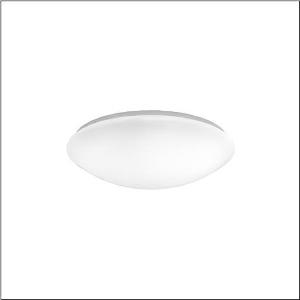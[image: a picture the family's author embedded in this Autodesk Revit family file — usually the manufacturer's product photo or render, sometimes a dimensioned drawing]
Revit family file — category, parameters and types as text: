
# Revit family: round_31_b_5pja130001a
name_source: partatom
category: Lighting Fixtures
units: mm (PartAtom-declared; Revit-internal decimal feet)

## family parameters
Cut with Voids When Loaded = No
Host = Face
Light Source = No
Part Type = Normal
Room Calculation Point = No
Round Connector Dimension = Use Diameter
Shared = No

## types (1)
- Round 31 B (1 x LED, 2700 lm, 21 W, 4000K)
    Apparent Load = 21 VA
    CIE Flux Codes = 42 71 89 88 100
    Color Rendering = 80
    Color Temperature = 4000K
    Default Elevation = 1800 mm
    Description = Round 31 B, wall and ceiling luminaire, primary optical cover: enclosure, of PMMA, light emission: direct distribution, primary light characteristic: symmetric, installation type: surface-mounted, LED, rated luminous flux: 2.700lm, luminous efficacy: 128lm/W, light colour: 840, colour temperature: 4000K, with terminal, 3-pole, max. 2.5mm², mains connection: 230V, AC, 50/60Hz, rated input power: 21W, luminaire housing, round, of steel, white, diameter: 360mm, height: 95mm, protection rating (complete): IP40, insulation class (complete): insulation class I (protective earthing), certification: CE, impact resistance: IK02, packaging unit: 1 piece
    Height = 95 mm
    Lamp = 1 x LED
    Lamp Light Flux = 2700 lm
    Lamp Power = 21 W
    Lamp count = 1
    Length = 360 mm
    Luminous efficacy = 129 lm/W
    Manufacturer = Siteco
    ModVariant = No
    Model = 5PJA130001A
    Mounting Place = Ceiling
    Mounting Type = Surface mounted
    Number of Poles = 1
    OnlyDefault = Yes
    Power Factor = 1
    Product Name = Round 31 B
    Product group = wall and ceiling luminaire
    ProductGroupID = 302
    Protection Class = Protection class I
    Protection Degree = IP 40
    RLX_Detail_Level = 1
    RLX_Emergency_Light_Flux = 0 lm
    RLX_Emergency_Type = 0
    RLX_Emergency_Type_DB = No
    RlxData = <blob elided: 10921 chars, md5=57c0cfa4>
    Socket = socket
    Standby Power = 0 W
    System Light Flux = 2700 lm
    System Power = 21 W
    Type Comments = Product without accessories
    Type Image = l_1258315.jpg
    URL = http://relux.com
    VarID = ---
    Voltage = 0 V
    Weight = 0.00 kg
    Width = 0 mm  [stored 0 ft]

note: [stored X ft] marks values corroborated as IEEE doubles in the binary element streams (Revit-internal decimal feet)

## geometry (parser evidence)
native form markers: Sweep x12
no freeform markers — native parametric forms only
